# Revit family: ASL Door Suite 75mm
name_source: partatom
category: Doors
revit_build: Autodesk Revit 2018 (Build: 20170223_1515(x64)
units: mm (PartAtom-declared; Revit-internal decimal feet)

## family parameters
Always vertical = Yes
Cut with Voids When Loaded = No
OmniClass Number = 23.25.20.14.11.11.17
OmniClass Title = Infill Panels
Room Calculation Point = No
Shared = No

## types (2) — shared parameters
Analytic Construction = <None>
Frame Thickness = 44 mm  [stored 0.144357 ft]
Frame Width = 75 mm
Glass Material = <By Category>
Manufacturer = Aluminate Solutions Limited
Material = <By Category>
Model = ASL Door Suite 75mm
Type Comments = ASL Door Suite 75mm
URL = http://www.productspec.net

## per-type parameters (varying)
| type | Head Depth | Kickplate High |
| 75mm Frame | 75 mm | 75 mm |
| 75mm Frame_100mm Head_100mm Kickplate | 100 mm  [stored 0.328084 ft] | 100 mm  [stored 0.328084 ft] |

note: [stored X ft] marks values corroborated as IEEE doubles in the binary element streams (Revit-internal decimal feet)

## geometry (parser evidence)
native form markers: Sweep x2
no freeform markers — native parametric forms only
